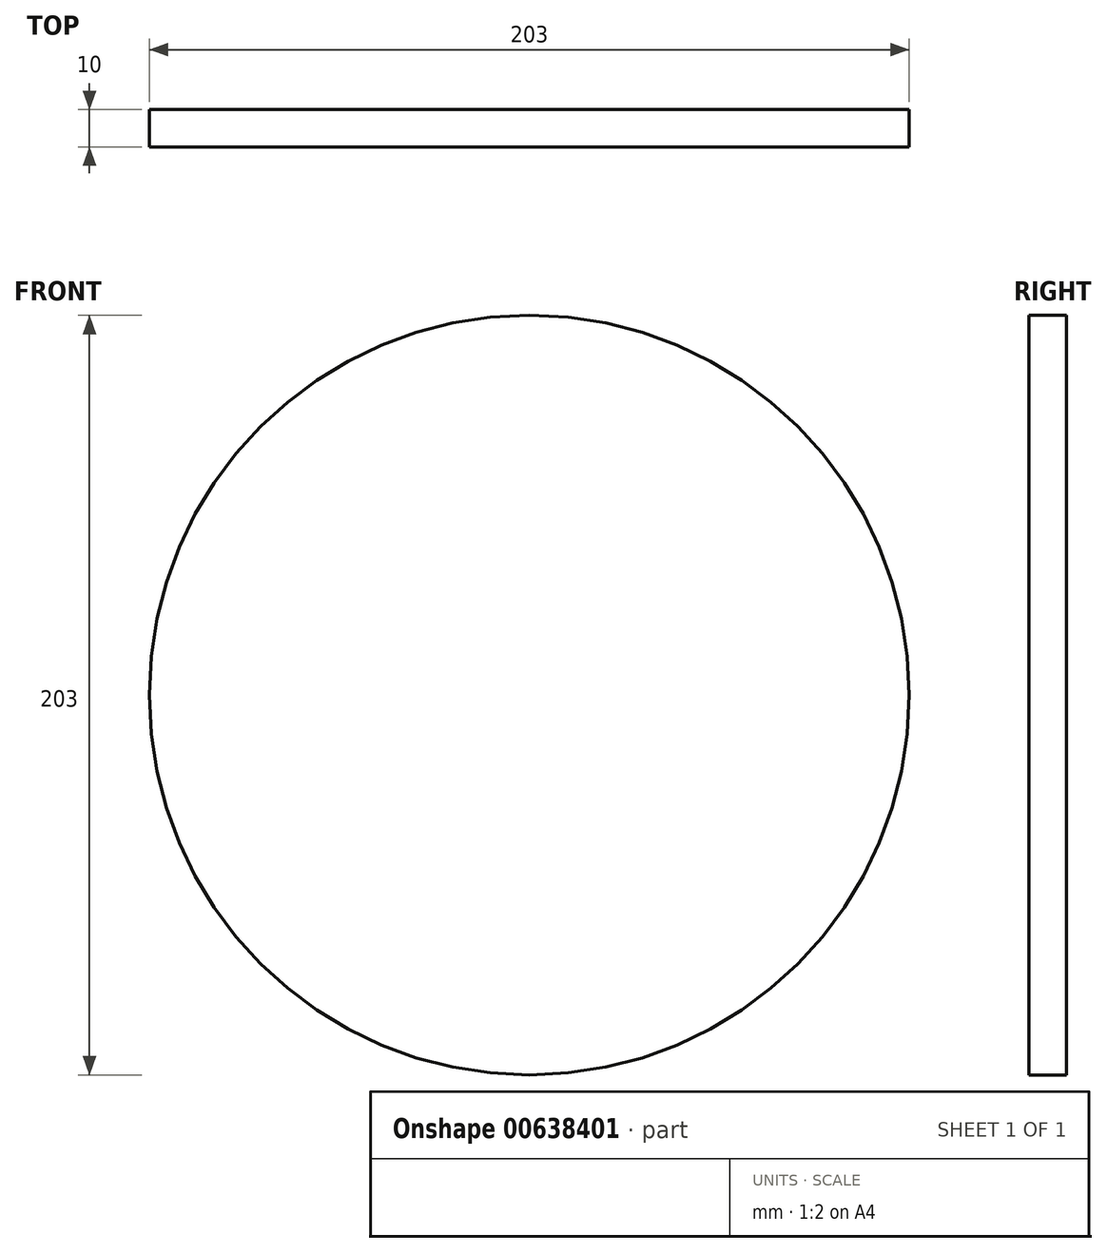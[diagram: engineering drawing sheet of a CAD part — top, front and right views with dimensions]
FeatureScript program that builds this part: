
annotation { "Feature Type Name" : "Feature", "Feature Type Description" : "" }
export const myFeature = defineFeature(function(context is Context, id is Id, definition is map)
    precondition{}
    {
        {
            var Q0;
            Q0=qCreatedBy(makeId("Front.planeOp"),FACE);
            var sketch = newSketch(context, id + "F0", { "sketchPlane" : qUnion([Q0])});
            skCircle(sketch, "E0", {"center": v(0, 0) * mm, "radius": 203.2 * mm});
            skSolve(sketch);
        }
        {
            var Q0;
            Q0=makeQuery(id+"F0.imprint","IMPRINT",FACE,{"disambiguationData":[TD([[makeQuery(id+"F0.imprint","IMPRINT",EDGE,{"derivedFrom":sQuery(id+"F0.wireOp",EDGE,"E0")}),1.0]])]});
            var sketch = newSketch(context, id + "F1", { "sketchPlane" : qUnion([Q0])});
            skCircle(sketch, "E1", {"center": v(0, 0) * mm, "radius": 101.5 * mm});
            skSolve(sketch);
        }
        {
            var Q0;
            Q0=sQuery(id+"F0.wireOp",EDGE,"E0");
            extrude(context, id + "F2", {"bodyType" : ToolBodyType.SURFACE, "surfaceEntities" : qUnion([Q0]), "depth" : 10 * mm, "offsetDistance" : 25 * mm});
        }
        {
            var Q0;
            Q0=makeQuery(id+"F1.imprint","IMPRINT",FACE,{"disambiguationData":[TD([[makeQuery(id+"F1.imprint","IMPRINT",EDGE,{"derivedFrom":sQuery(id+"F1.wireOp",EDGE,"E1")}),1.0]])]});
            extrude(context, id + "F3", {"entities" : qUnion([Q0]), "depth" : 10 * mm, "offsetDistance" : 25 * mm});
        }
    });
